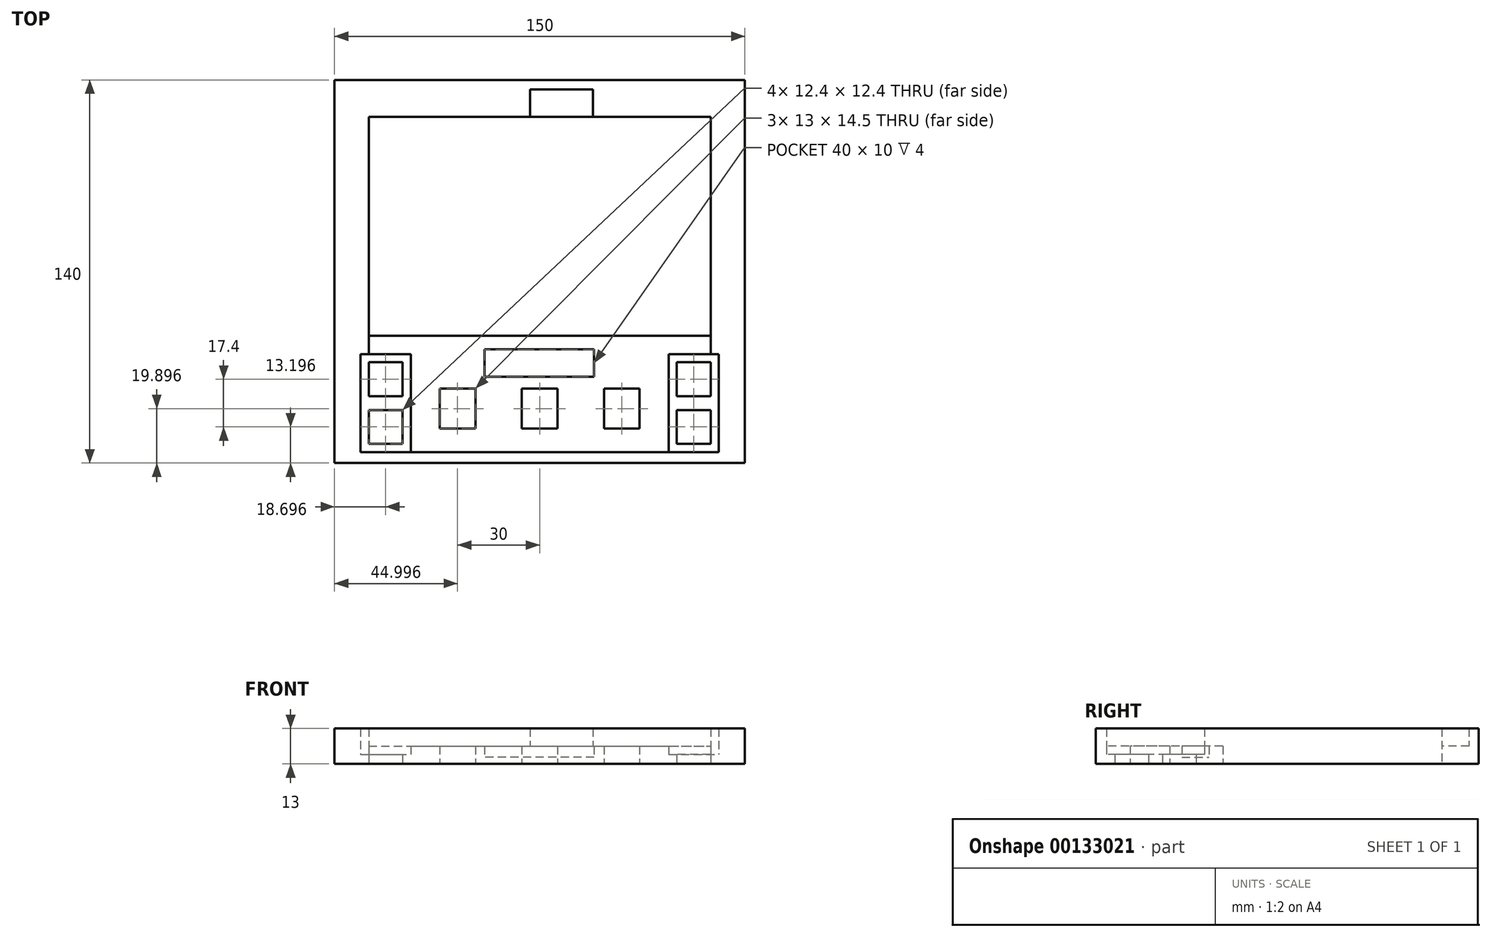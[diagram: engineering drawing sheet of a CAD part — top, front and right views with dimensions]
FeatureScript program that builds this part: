
annotation { "Feature Type Name" : "Feature", "Feature Type Description" : "" }
export const myFeature = defineFeature(function(context is Context, id is Id, definition is map)
    precondition{}
    {
        {
            var Q0;
            Q0=qCreatedBy(makeId("Top.planeOp"),FACE);
            var sketch = newSketch(context, id + "F0", { "sketchPlane" : qUnion([Q0])});
            skLineSegment(sketch, "E0.bottom", {"start": v(-79.53, 76.7) * mm, "end": v(70.47, 76.7) * mm});
            skLineSegment(sketch, "E0.top", {"start": v(-79.53, -63.3) * mm, "end": v(70.47, -63.3) * mm});
            skLineSegment(sketch, "E0.left", {"start": v(-79.53, 76.7) * mm, "end": v(-79.53, -63.3) * mm});
            skLineSegment(sketch, "E0.right", {"start": v(70.47, 76.7) * mm, "end": v(70.47, -63.3) * mm});
            skLineSegment(sketch, "E1.bottom", {"start": v(-67.03, 63.2) * mm, "end": v(57.97, 63.2) * mm});
            skLineSegment(sketch, "E1.top", {"start": v(-67.03, -16.8) * mm, "end": v(57.97, -16.8) * mm});
            skLineSegment(sketch, "E1.left", {"start": v(-67.03, 63.2) * mm, "end": v(-67.03, -16.8) * mm});
            skLineSegment(sketch, "E1.right", {"start": v(57.97, 63.2) * mm, "end": v(57.97, -16.8) * mm});
            skLineSegment(sketch, "E2", {"start": v(-67.03, 63.2) * mm, "end": v(-79.53, 63.2) * mm, "construction": true});
            skLineSegment(sketch, "E3.bottom", {"start": v(-67.03, -26.5) * mm, "end": v(-54.63, -26.5) * mm});
            skLineSegment(sketch, "E3.top", {"start": v(-67.03, -38.9) * mm, "end": v(-54.63, -38.9) * mm});
            skLineSegment(sketch, "E3.left", {"start": v(-67.03, -26.5) * mm, "end": v(-67.03, -38.9) * mm});
            skLineSegment(sketch, "E3.right", {"start": v(-54.63, -26.5) * mm, "end": v(-54.63, -38.9) * mm});
            skPoint(sketch, "E4.oppositeSnap0", {"position": v(-54.63, -32.7) * mm});
            skLineSegment(sketch, "E5.bottom", {"start": v(45.57, -26.5) * mm, "end": v(57.97, -26.5) * mm});
            skLineSegment(sketch, "E5.top", {"start": v(45.57, -38.9) * mm, "end": v(57.97, -38.9) * mm});
            skLineSegment(sketch, "E5.left", {"start": v(45.57, -26.5) * mm, "end": v(45.57, -38.9) * mm});
            skLineSegment(sketch, "E5.right", {"start": v(57.97, -26.5) * mm, "end": v(57.97, -38.9) * mm});
            skLineSegment(sketch, "E6.bottom", {"start": v(57.97, -43.9) * mm, "end": v(45.57, -43.9) * mm});
            skLineSegment(sketch, "E6.top", {"start": v(57.97, -56.3) * mm, "end": v(45.57, -56.3) * mm});
            skLineSegment(sketch, "E6.left", {"start": v(57.97, -43.9) * mm, "end": v(57.97, -56.3) * mm});
            skLineSegment(sketch, "E6.right", {"start": v(45.57, -43.9) * mm, "end": v(45.57, -56.3) * mm});
            skLineSegment(sketch, "E7.bottom", {"start": v(-67.03, -43.9) * mm, "end": v(-54.63, -43.9) * mm});
            skLineSegment(sketch, "E7.top", {"start": v(-67.03, -56.3) * mm, "end": v(-54.63, -56.3) * mm});
            skLineSegment(sketch, "E7.left", {"start": v(-67.03, -43.9) * mm, "end": v(-67.03, -56.3) * mm});
            skLineSegment(sketch, "E7.right", {"start": v(-54.63, -43.9) * mm, "end": v(-54.63, -56.3) * mm});
            skLineSegment(sketch, "E8.bottom", {"start": v(-41.03, -36.15) * mm, "end": v(-28.03, -36.15) * mm});
            skLineSegment(sketch, "E8.top", {"start": v(-41.03, -50.65) * mm, "end": v(-28.03, -50.65) * mm});
            skLineSegment(sketch, "E8.left", {"start": v(-41.03, -36.15) * mm, "end": v(-41.03, -50.65) * mm});
            skLineSegment(sketch, "E8.right", {"start": v(-28.03, -36.15) * mm, "end": v(-28.03, -50.65) * mm});
            skLineSegment(sketch, "E9.bottom", {"start": v(-11.03, -36.15) * mm, "end": v(1.97, -36.15) * mm});
            skLineSegment(sketch, "E9.top", {"start": v(-11.03, -50.65) * mm, "end": v(1.97, -50.65) * mm});
            skLineSegment(sketch, "E9.left", {"start": v(-11.03, -36.15) * mm, "end": v(-11.03, -50.65) * mm});
            skLineSegment(sketch, "E9.right", {"start": v(1.97, -36.15) * mm, "end": v(1.97, -50.65) * mm});
            skLineSegment(sketch, "E10.bottom", {"start": v(18.97, -36.15) * mm, "end": v(31.97, -36.15) * mm});
            skLineSegment(sketch, "E10.top", {"start": v(18.97, -50.65) * mm, "end": v(31.97, -50.65) * mm});
            skLineSegment(sketch, "E10.left", {"start": v(18.97, -36.15) * mm, "end": v(18.97, -50.65) * mm});
            skLineSegment(sketch, "E10.right", {"start": v(31.97, -36.15) * mm, "end": v(31.97, -50.65) * mm});
            skLineSegment(sketch, "E11", {"start": v(-28.03, -36.15) * mm, "end": v(-11.03, -36.15) * mm, "construction": true});
            skLineSegment(sketch, "E12", {"start": v(1.97, -36.15) * mm, "end": v(18.97, -36.15) * mm, "construction": true});
            skLineSegment(sketch, "E13", {"start": v(-67.03, -56.3) * mm, "end": v(-79.53, -56.3) * mm, "construction": true});
            skLineSegment(sketch, "E14", {"start": v(57.97, -56.3) * mm, "end": v(70.47, -56.3) * mm, "construction": true});
            skLineSegment(sketch, "E15.bottom", {"start": v(-70.03, -23.5) * mm, "end": v(-51.63, -23.5) * mm});
            skLineSegment(sketch, "E15.top", {"start": v(-70.03, -59.3) * mm, "end": v(-51.63, -59.3) * mm});
            skLineSegment(sketch, "E15.left", {"start": v(-70.03, -23.5) * mm, "end": v(-70.03, -59.3) * mm});
            skLineSegment(sketch, "E15.right", {"start": v(-51.63, -23.5) * mm, "end": v(-51.63, -59.3) * mm});
            skLineSegment(sketch, "E16.bottom", {"start": v(40.57, -23.5) * mm, "end": v(62.97, -23.5) * mm});
            skLineSegment(sketch, "E16.top", {"start": v(40.57, -59.3) * mm, "end": v(62.97, -59.3) * mm});
            skLineSegment(sketch, "E16.left", {"start": v(40.57, -23.5) * mm, "end": v(40.57, -59.3) * mm});
            skLineSegment(sketch, "E16.right", {"start": v(62.97, -23.5) * mm, "end": v(62.97, -59.3) * mm});
            skLineSegment(sketch, "E17", {"start": v(-54.63, -56.3) * mm, "end": v(-54.63, -59.3) * mm, "construction": true});
            skLineSegment(sketch, "E18", {"start": v(-54.63, -26.5) * mm, "end": v(-54.63, -23.5) * mm, "construction": true});
            skLineSegment(sketch, "E19", {"start": v(45.57, -26.5) * mm, "end": v(45.57, -23.5) * mm, "construction": true});
            skLineSegment(sketch, "E20", {"start": v(45.57, -56.3) * mm, "end": v(45.57, -59.3) * mm, "construction": true});
            skLineSegment(sketch, "E21", {"start": v(57.97, -26.5) * mm, "end": v(62.97, -26.5) * mm, "construction": true});
            skLineSegment(sketch, "E22", {"start": v(45.57, -26.5) * mm, "end": v(40.57, -26.5) * mm, "construction": true});
            skLineSegment(sketch, "E23", {"start": v(-67.03, -26.5) * mm, "end": v(-70.03, -26.5) * mm, "construction": true});
            skLineSegment(sketch, "E24", {"start": v(-54.63, -26.5) * mm, "end": v(-51.63, -26.5) * mm, "construction": true});
            skLineSegment(sketch, "E25", {"start": v(57.97, -16.8) * mm, "end": v(57.97, -23.5) * mm, "construction": true});
            skLineSegment(sketch, "E26", {"start": v(-11.03, -50.65) * mm, "end": v(-11.03, -63.3) * mm, "construction": true});
            skLineSegment(sketch, "E27", {"start": v(-41.03, -43.4) * mm, "end": v(-41.03, -63.3) * mm, "construction": true});
            skLineSegment(sketch, "E28", {"start": v(-51.63, -59.3) * mm, "end": v(-51.63, -63.3) * mm, "construction": true});
            skLineSegment(sketch, "E29", {"start": v(62.97, -59.3) * mm, "end": v(62.97, -63.3) * mm, "construction": true});
            skLineSegment(sketch, "E30", {"start": v(-67.03, 63.2) * mm, "end": v(-67.03, 76.7) * mm, "construction": true});
            skLineSegment(sketch, "E31.bottom", {"start": v(-24.63, -21.8) * mm, "end": v(15.37, -21.8) * mm});
            skLineSegment(sketch, "E31.top", {"start": v(-24.63, -31.8) * mm, "end": v(15.37, -31.8) * mm});
            skLineSegment(sketch, "E31.left", {"start": v(-24.63, -21.8) * mm, "end": v(-24.63, -31.8) * mm});
            skLineSegment(sketch, "E31.right", {"start": v(15.37, -21.8) * mm, "end": v(15.37, -31.8) * mm});
            skLineSegment(sketch, "E32", {"start": v(15.37, -21.8) * mm, "end": v(15.37, -16.8) * mm, "construction": true});
            skLineSegment(sketch, "E33", {"start": v(-24.63, -31.8) * mm, "end": v(-51.63, -31.8) * mm, "construction": true});
            skSolve(sketch);
        }
        {
            var Q0;
            Q0=makeQuery(id+"F0.imprint","IMPRINT",FACE,{"disambiguationData":[TD([[makeQuery(id+"F0.imprint","IMPRINT",EDGE,{"derivedFrom":sQuery(id+"F0.wireOp",EDGE,"E0.bottom")}),-1.0]])]});
            var Q1;
            Q1=makeQuery(id+"F0.imprint","IMPRINT",FACE,{"disambiguationData":[TD([[makeQuery(id+"F0.imprint","IMPRINT",EDGE,{"derivedFrom":sQuery(id+"F0.wireOp",EDGE,"E3.bottom")}),1.0]])]});
            var Q2;
            Q2=makeQuery(id+"F0.imprint","IMPRINT",FACE,{"disambiguationData":[TD([[makeQuery(id+"F0.imprint","IMPRINT",EDGE,{"derivedFrom":sQuery(id+"F0.wireOp",EDGE,"E5.bottom")}),1.0]])]});
            var Q3;
            Q3=makeQuery(id+"F0.imprint","IMPRINT",FACE,{"disambiguationData":[TD([[makeQuery(id+"F0.imprint","IMPRINT",EDGE,{"derivedFrom":sQuery(id+"F0.wireOp",EDGE,"E31.bottom")}),-1.0]])]});
            extrude(context, id + "F1", {"entities" : qUnion([Q0, Q1, Q2, Q3]), "depth" : 2.5 * mm});
        }
        {
            var Q0;
            Q0=makeQuery(id+"F0.imprint","IMPRINT",FACE,{"disambiguationData":[TD([[makeQuery(id+"F0.imprint","IMPRINT",EDGE,{"derivedFrom":sQuery(id+"F0.wireOp",EDGE,"E0.bottom")}),-1.0]])]});
            var Q1;
            Q1=makeQuery(id+"F0.imprint","IMPRINT",FACE,{"disambiguationData":[TD([[makeQuery(id+"F0.imprint","IMPRINT",EDGE,{"derivedFrom":sQuery(id+"F0.wireOp",EDGE,"E3.bottom")}),1.0]])]});
            var Q2;
            Q2=makeQuery(id+"F0.imprint","IMPRINT",FACE,{"disambiguationData":[TD([[makeQuery(id+"F0.imprint","IMPRINT",EDGE,{"derivedFrom":sQuery(id+"F0.wireOp",EDGE,"E5.bottom")}),1.0]])]});
            extrude(context, id + "F2", {"entities" : qUnion([Q0, Q1, Q2]), "operationType" : NewBodyOperationType.ADD, "depth" : 3.5 * mm});
        }
        {
            var Q0;
            Q0=makeQuery(id+"F2.opExtrude","CAP_FACE",FACE,{"disambiguationData":[OSD([sQuery(id+"F0.wireOp",EDGE,"E0.bottom"),sQuery(id+"F0.wireOp",EDGE,"E0.top"),sQuery(id+"F0.wireOp",EDGE,"E0.left"),sQuery(id+"F0.wireOp",EDGE,"E0.right"),sQuery(id+"F0.wireOp",EDGE,"E1.bottom"),sQuery(id+"F0.wireOp",EDGE,"E1.top"),sQuery(id+"F0.wireOp",EDGE,"E1.left"),sQuery(id+"F0.wireOp",EDGE,"E1.right"),sQuery(id+"F0.wireOp",EDGE,"E3.bottom"),sQuery(id+"F0.wireOp",EDGE,"E3.top"),sQuery(id+"F0.wireOp",EDGE,"E3.left"),sQuery(id+"F0.wireOp",EDGE,"E3.right"),sQuery(id+"F0.wireOp",EDGE,"E5.bottom"),sQuery(id+"F0.wireOp",EDGE,"E5.top"),sQuery(id+"F0.wireOp",EDGE,"E5.left"),sQuery(id+"F0.wireOp",EDGE,"E5.right"),sQuery(id+"F0.wireOp",EDGE,"E6.bottom"),sQuery(id+"F0.wireOp",EDGE,"E6.top"),sQuery(id+"F0.wireOp",EDGE,"E6.left"),sQuery(id+"F0.wireOp",EDGE,"E6.right"),sQuery(id+"F0.wireOp",EDGE,"E7.bottom"),sQuery(id+"F0.wireOp",EDGE,"E7.top"),sQuery(id+"F0.wireOp",EDGE,"E7.left"),sQuery(id+"F0.wireOp",EDGE,"E7.right"),sQuery(id+"F0.wireOp",EDGE,"E8.bottom"),sQuery(id+"F0.wireOp",EDGE,"E8.top"),sQuery(id+"F0.wireOp",EDGE,"E8.left"),sQuery(id+"F0.wireOp",EDGE,"E8.right"),sQuery(id+"F0.wireOp",EDGE,"E9.bottom"),sQuery(id+"F0.wireOp",EDGE,"E9.top"),sQuery(id+"F0.wireOp",EDGE,"E9.left"),sQuery(id+"F0.wireOp",EDGE,"E9.right"),sQuery(id+"F0.wireOp",EDGE,"E10.bottom"),sQuery(id+"F0.wireOp",EDGE,"E10.top"),sQuery(id+"F0.wireOp",EDGE,"E10.left"),sQuery(id+"F0.wireOp",EDGE,"E10.right"),sQuery(id+"F0.wireOp",EDGE,"E31.bottom"),sQuery(id+"F0.wireOp",EDGE,"E31.top"),sQuery(id+"F0.wireOp",EDGE,"E31.left"),sQuery(id+"F0.wireOp",EDGE,"E31.right")])],"isStart":false});
            var sketch = newSketch(context, id + "F3", { "sketchPlane" : qUnion([Q0])});
            skLineSegment(sketch, "E34.bottom", {"start": v(-70.03, -23.5) * mm, "end": v(-51.63, -23.5) * mm});
            skLineSegment(sketch, "E34.top", {"start": v(-70.03, -59.3) * mm, "end": v(-51.63, -59.3) * mm});
            skLineSegment(sketch, "E34.left", {"start": v(-70.03, -23.5) * mm, "end": v(-70.03, -59.3) * mm});
            skLineSegment(sketch, "E34.right", {"start": v(-51.63, -23.5) * mm, "end": v(-51.63, -59.3) * mm});
            skLineSegment(sketch, "E35.bottom", {"start": v(42.57, -23.5) * mm, "end": v(60.97, -23.5) * mm});
            skLineSegment(sketch, "E35.top", {"start": v(42.57, -59.3) * mm, "end": v(60.97, -59.3) * mm});
            skLineSegment(sketch, "E35.left", {"start": v(42.57, -23.5) * mm, "end": v(42.57, -59.3) * mm});
            skLineSegment(sketch, "E35.right", {"start": v(60.97, -23.5) * mm, "end": v(60.97, -59.3) * mm});
            skPoint(sketch, "E36.endSnap0", {"position": v(-60.83, -23.5) * mm});
            skLineSegment(sketch, "E37", {"start": v(45.57, -26.5) * mm, "end": v(45.57, -23.5) * mm, "construction": true});
            skLineSegment(sketch, "E38", {"start": v(-54.63, -26.5) * mm, "end": v(-54.63, -23.5) * mm, "construction": true});
            skLineSegment(sketch, "E39", {"start": v(-67.03, -26.5) * mm, "end": v(-67.03, -23.5) * mm, "construction": true});
            skLineSegment(sketch, "E40", {"start": v(-67.03, -26.5) * mm, "end": v(-70.03, -26.5) * mm, "construction": true});
            skLineSegment(sketch, "E41", {"start": v(-54.63, -56.3) * mm, "end": v(-54.63, -59.3) * mm, "construction": true});
            skLineSegment(sketch, "E42", {"start": v(-54.63, -56.3) * mm, "end": v(-51.63, -56.3) * mm, "construction": true});
            skLineSegment(sketch, "E43", {"start": v(57.97, -26.5) * mm, "end": v(60.97, -26.5) * mm, "construction": true});
            skLineSegment(sketch, "E44", {"start": v(57.97, -26.5) * mm, "end": v(57.97, -23.5) * mm, "construction": true});
            skLineSegment(sketch, "E45", {"start": v(57.97, -56.3) * mm, "end": v(57.97, -59.3) * mm, "construction": true});
            skLineSegment(sketch, "E46", {"start": v(57.97, -56.3) * mm, "end": v(60.97, -56.3) * mm, "construction": true});
            skLineSegment(sketch, "E47", {"start": v(45.57, -26.5) * mm, "end": v(42.57, -26.5) * mm, "construction": true});
            skSolve(sketch);
        }
        {
            var Q0;
            Q0=makeQuery(id+"F3.imprint","IMPRINT",FACE,{"disambiguationData":[TD([[makeQuery(id+"F3.imprint","IMPRINT",EDGE,{"derivedFrom":sQuery(id+"F3.wireOp",EDGE,"E34.bottom")}),1.0]])]});
            extrude(context, id + "F4", {"entities" : qUnion([Q0]), "operationType" : NewBodyOperationType.ADD, "depth" : 3 * mm});
        }
        {
            var Q0;
            Q0=makeQuery(id+"F4.opExtrude","CAP_FACE",FACE,{"disambiguationData":[OSD([sQuery(id+"F0.wireOp",EDGE,"E0.bottom"),sQuery(id+"F0.wireOp",EDGE,"E0.top"),sQuery(id+"F0.wireOp",EDGE,"E0.left"),sQuery(id+"F0.wireOp",EDGE,"E0.right"),sQuery(id+"F0.wireOp",EDGE,"E1.bottom"),sQuery(id+"F0.wireOp",EDGE,"E1.top"),sQuery(id+"F0.wireOp",EDGE,"E1.left"),sQuery(id+"F0.wireOp",EDGE,"E1.right"),sQuery(id+"F0.wireOp",EDGE,"E8.bottom"),sQuery(id+"F0.wireOp",EDGE,"E8.top"),sQuery(id+"F0.wireOp",EDGE,"E8.left"),sQuery(id+"F0.wireOp",EDGE,"E8.right"),sQuery(id+"F0.wireOp",EDGE,"E9.bottom"),sQuery(id+"F0.wireOp",EDGE,"E9.top"),sQuery(id+"F0.wireOp",EDGE,"E9.left"),sQuery(id+"F0.wireOp",EDGE,"E9.right"),sQuery(id+"F0.wireOp",EDGE,"E10.bottom"),sQuery(id+"F0.wireOp",EDGE,"E10.top"),sQuery(id+"F0.wireOp",EDGE,"E10.left"),sQuery(id+"F0.wireOp",EDGE,"E10.right"),sQuery(id+"F3.wireOp",EDGE,"E34.bottom"),sQuery(id+"F3.wireOp",EDGE,"E34.top"),sQuery(id+"F3.wireOp",EDGE,"E34.left"),sQuery(id+"F3.wireOp",EDGE,"E34.right"),sQuery(id+"F3.wireOp",EDGE,"E35.bottom"),sQuery(id+"F3.wireOp",EDGE,"E35.top"),sQuery(id+"F3.wireOp",EDGE,"E35.left"),sQuery(id+"F3.wireOp",EDGE,"E35.right")])],"isStart":false});
            var sketch = newSketch(context, id + "F5", { "sketchPlane" : qUnion([Q0])});
            skLineSegment(sketch, "E48.bottom", {"start": v(-67.03, -16.8) * mm, "end": v(-56.53, -16.8) * mm});
            skLineSegment(sketch, "E48.top", {"start": v(-67.03, -23.5) * mm, "end": v(-56.53, -23.5) * mm});
            skLineSegment(sketch, "E48.left", {"start": v(-67.03, -16.8) * mm, "end": v(-67.03, -23.5) * mm});
            skLineSegment(sketch, "E49.bottom", {"start": v(57.97, -16.8) * mm, "end": v(47.47, -16.8) * mm});
            skLineSegment(sketch, "E49.top", {"start": v(57.97, -23.5) * mm, "end": v(47.47, -23.5) * mm});
            skLineSegment(sketch, "E49.left", {"start": v(57.97, -16.8) * mm, "end": v(57.97, -23.5) * mm});
            skLineSegment(sketch, "E50.top", {"start": v(-51.63, -59.3) * mm, "end": v(42.57, -59.3) * mm});
            skLineSegment(sketch, "E50.left", {"start": v(-51.63, -23.5) * mm, "end": v(-51.63, -59.3) * mm});
            skLineSegment(sketch, "E50.right", {"start": v(42.57, -23.5) * mm, "end": v(42.57, -59.3) * mm});
            skLineSegment(sketch, "E51", {"start": v(6.7, -59.3) * mm, "end": v(6.7, -16.8) * mm, "construction": true});
            skLineSegment(sketch, "E52", {"start": v(57.97, 63.2) * mm, "end": v(57.97, 76.7) * mm, "construction": true});
            skLineSegment(sketch, "E53", {"start": v(70.47, 76.7) * mm, "end": v(14.97, 76.7) * mm, "construction": true});
            skLineSegment(sketch, "E54", {"start": v(14.97, 76.7) * mm, "end": v(-8.03, 76.7) * mm, "construction": true});
            skLineSegment(sketch, "E55", {"start": v(-8.03, 76.7) * mm, "end": v(-79.53, 76.7) * mm, "construction": true});
            skLineSegment(sketch, "E56", {"start": v(-8.03, 76.7) * mm, "end": v(-8.03, 63.2) * mm, "construction": true});
            skLineSegment(sketch, "E57", {"start": v(14.97, 76.7) * mm, "end": v(14.97, 63.2) * mm, "construction": true});
            skLineSegment(sketch, "E58", {"start": v(14.97, 63.2) * mm, "end": v(14.97, 73.2) * mm, "construction": true});
            skLineSegment(sketch, "E59", {"start": v(-8.03, 73.2) * mm, "end": v(-8.03, 63.2) * mm, "construction": true});
            skLineSegment(sketch, "E60.bottom", {"start": v(-8.03, 73.2) * mm, "end": v(14.97, 73.2) * mm});
            skLineSegment(sketch, "E60.top", {"start": v(-8.03, 63.2) * mm, "end": v(14.97, 63.2) * mm});
            skLineSegment(sketch, "E60.left", {"start": v(-8.03, 73.2) * mm, "end": v(-8.03, 63.2) * mm});
            skLineSegment(sketch, "E60.right", {"start": v(14.97, 73.2) * mm, "end": v(14.97, 63.2) * mm});
            skLineSegment(sketch, "E61.bottom", {"start": v(-56.53, -23.5) * mm, "end": v(-67.03, -23.5) * mm});
            skLineSegment(sketch, "E61.top", {"start": v(-56.53, -16.8) * mm, "end": v(-67.03, -16.8) * mm});
            skLineSegment(sketch, "E61.left", {"start": v(-56.53, -23.5) * mm, "end": v(-56.53, -16.8) * mm});
            skLineSegment(sketch, "E61.right", {"start": v(-67.03, -23.5) * mm, "end": v(-67.03, -16.8) * mm});
            skLineSegment(sketch, "E62.bottom", {"start": v(47.47, -23.5) * mm, "end": v(57.97, -23.5) * mm});
            skLineSegment(sketch, "E62.top", {"start": v(47.47, -16.8) * mm, "end": v(57.97, -16.8) * mm});
            skLineSegment(sketch, "E62.left", {"start": v(47.47, -23.5) * mm, "end": v(47.47, -16.8) * mm});
            skLineSegment(sketch, "E62.right", {"start": v(57.97, -23.5) * mm, "end": v(57.97, -16.8) * mm});
            skSolve(sketch);
        }
        {
            var Q0;
            Q0=makeQuery(id+"F5.imprint","IMPRINT",FACE,{"disambiguationData":[TD([[makeQuery(id+"F5.imprint","IMPRINT",EDGE,{"derivedFrom":sQuery(id+"F5.wireOp",EDGE,"E61.bottom")}),1.0]])]});
            var Q1;
            Q1=makeQuery(id+"F5.imprint","IMPRINT",FACE,{"disambiguationData":[TD([[makeQuery(id+"F5.imprint","IMPRINT",EDGE,{"derivedFrom":sQuery(id+"F5.wireOp",EDGE,"E62.bottom")}),1.0]])]});
            var Q2;
            Q2=makeQuery(id+"F5.imprint","IMPRINT",FACE,{"disambiguationData":[TD([[makeQuery(id+"F5.imprint","IMPRINT",EDGE,{"derivedFrom":sQuery(id+"F5.wireOp",EDGE,"E50.top")}),-1.0]])]});
            extrude(context, id + "F6", {"entities" : qUnion([Q0, Q1, Q2]), "operationType" : NewBodyOperationType.ADD, "depth" : 6.5 * mm});
        }
    });
